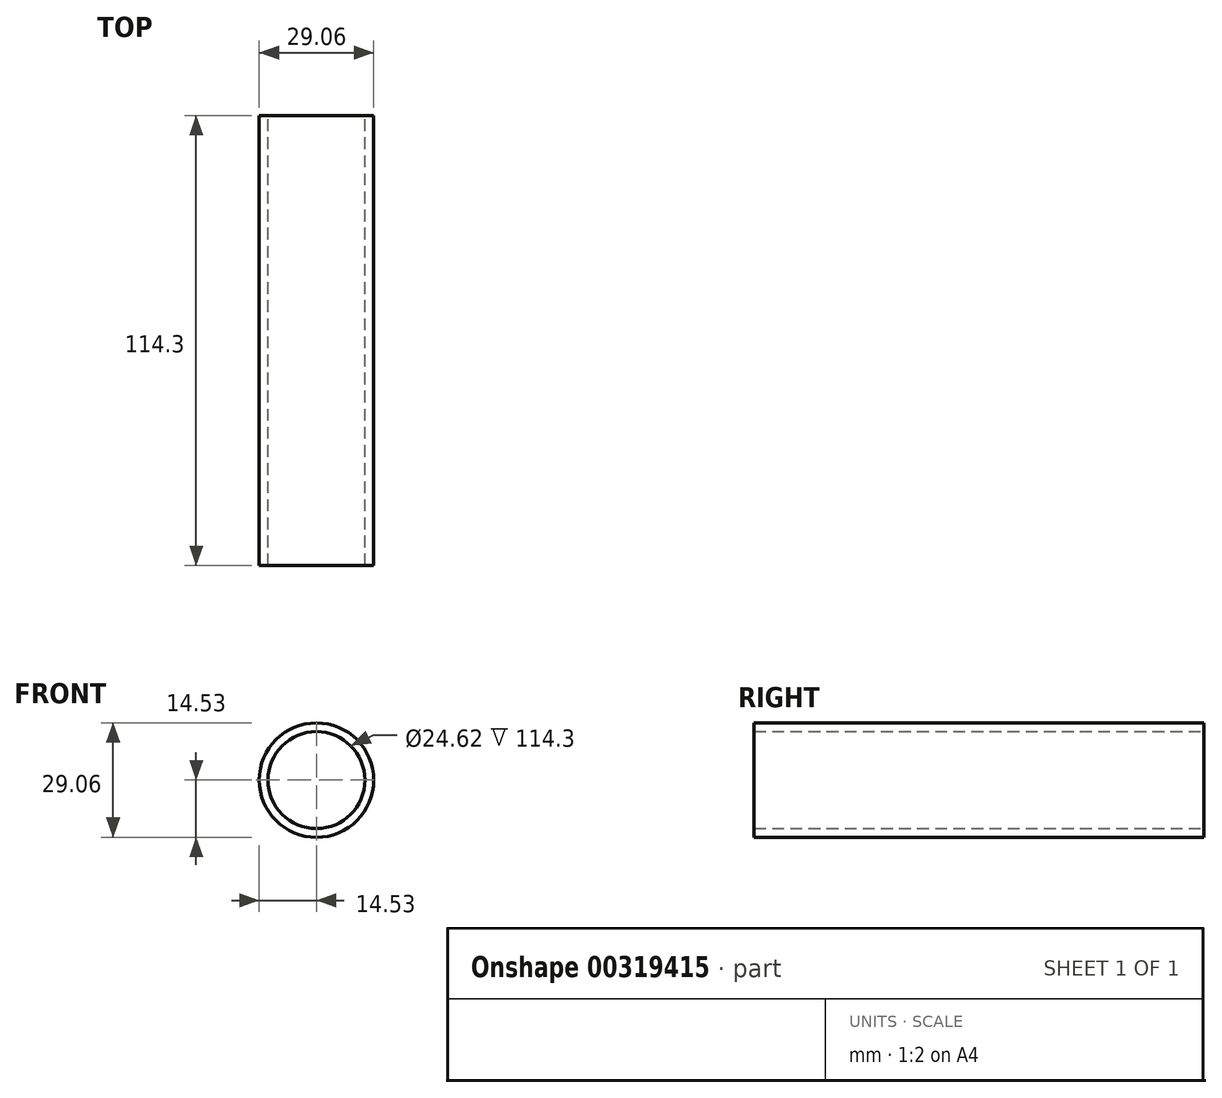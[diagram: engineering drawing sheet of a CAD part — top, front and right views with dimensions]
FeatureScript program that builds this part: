
annotation { "Feature Type Name" : "Feature", "Feature Type Description" : "" }
export const myFeature = defineFeature(function(context is Context, id is Id, definition is map)
    precondition{}
    {
        {
            var Q0;
            Q0=qCreatedBy(makeId("Front.planeOp"),FACE);
            var sketch = newSketch(context, id + "F0", { "sketchPlane" : qUnion([Q0])});
            skCircle(sketch, "E0", {"center": v(0, 0) * mm, "radius": 14.53 * mm});
            skCircle(sketch, "E1", {"center": v(0, 0) * mm, "radius": 12.31 * mm});
            skSolve(sketch);
        }
        {
            var Q0;
            Q0 = qSketchRegion(id + "F0", true);
            extrude(context, id + "F1", {"entities" : qUnion([Q0]), "depth" : 114.3 * mm});
        }
    });
